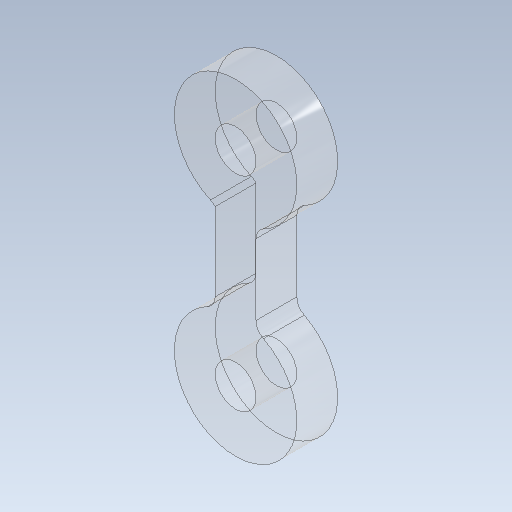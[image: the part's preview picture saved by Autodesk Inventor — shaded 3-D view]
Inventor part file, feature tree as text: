
AUTODESK INVENTOR PART (.ipt)
format: ipt  version: 2020.2 (Build 242310000, 310)  size: 133,120 bytes
history: native  units: mm
features: other x1, extrude x1, sketch x1
ambient origin geometry x8: Origin, YZ Plane, XZ Plane, XY Plane, X Axis, Y Axis, Z Axis, Center Point
bodies: Body1 (feature_tree)
feature tree (3):
  other  "ソリッド1"
  extrude  "押し出し1"  Depth=3.0mm TaperAngle=0.0deg
  sketch  "スケッチ1"
